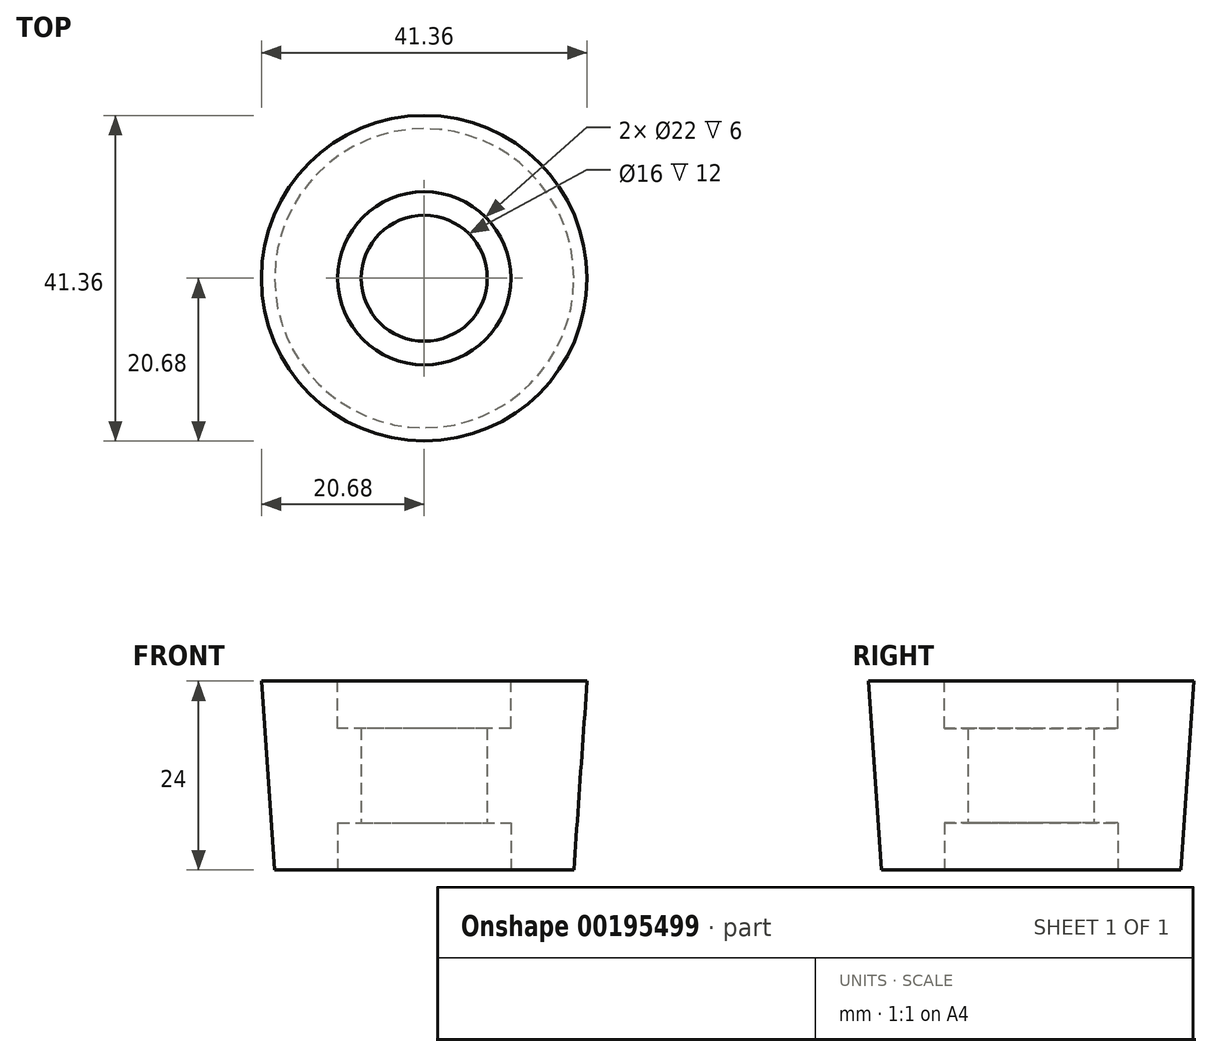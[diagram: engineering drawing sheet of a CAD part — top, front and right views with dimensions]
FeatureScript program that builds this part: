
annotation { "Feature Type Name" : "Feature", "Feature Type Description" : "" }
export const myFeature = defineFeature(function(context is Context, id is Id, definition is map)
    precondition{}
    {
        {
            var Q0;
            Q0=qCreatedBy(makeId("Top.planeOp"),FACE);
            var sketch = newSketch(context, id + "F0", { "sketchPlane" : qUnion([Q0])});
            skCircle(sketch, "E0", {"center": v(0, 0) * mm, "radius": 19 * mm});
            skSolve(sketch);
        }
        {
            var Q0;
            Q0=makeQuery(id+"F0.imprint","IMPRINT",FACE,{"disambiguationData":[TD([[makeQuery(id+"F0.imprint","IMPRINT",EDGE,{"derivedFrom":sQuery(id+"F0.wireOp",EDGE,"E0")}),1.0]])]});
            extrude(context, id + "F1", {"entities" : qUnion([Q0]), "depth" : 24 * mm, "hasDraft" : true, "draftAngle" : 4 * degree});
        }
        {
            var Q0;
            Q0=makeQuery(id+"F1.opExtrude","CAP_FACE",FACE,{"disambiguationData":[OSD([sQuery(id+"F0.wireOp",EDGE,"E0")])],"isStart":true});
            var sketch = newSketch(context, id + "F2", { "sketchPlane" : qUnion([Q0])});
            skCircle(sketch, "E1", {"center": v(0, 0) * mm, "radius": 8 * mm});
            skCircle(sketch, "E2", {"center": v(0, 0) * mm, "radius": 11 * mm});
            skSolve(sketch);
        }
        {
            var Q0;
            Q0=makeQuery(id+"F2.imprint","IMPRINT",FACE,{"disambiguationData":[TD([[makeQuery(id+"F2.imprint","IMPRINT",EDGE,{"derivedFrom":sQuery(id+"F2.wireOp",EDGE,"E1")}),1.0]])]});
            extrude(context, id + "F3", {"entities" : qUnion([Q0]), "operationType" : NewBodyOperationType.REMOVE, "endBound" : BoundingType.THROUGH_ALL, "oppositeDirection" : true, "depth" : 25 * mm});
        }
        {
            var Q0;
            Q0 = qSketchRegion(id + "F2", true);
            extrude(context, id + "F4", {"entities" : qUnion([Q0]), "operationType" : NewBodyOperationType.REMOVE, "oppositeDirection" : true, "depth" : 6 * mm});
        }
        {
            var Q0;
            Q0=makeQuery(id+"F1.opExtrude","CAP_FACE",FACE,{"disambiguationData":[OSD([sQuery(id+"F0.wireOp",EDGE,"E0")])],"isStart":false});
            var sketch = newSketch(context, id + "F5", { "sketchPlane" : qUnion([Q0])});
            skCircle(sketch, "E3", {"center": v(0, 0) * mm, "radius": 11 * mm});
            skSolve(sketch);
        }
        {
            var Q0;
            Q0=makeQuery(id+"F5.imprint","IMPRINT",FACE,{"disambiguationData":[TD([[makeQuery(id+"F5.imprint","IMPRINT",EDGE,{"derivedFrom":sQuery(id+"F5.wireOp",EDGE,"E3")}),1.0]])]});
            extrude(context, id + "F6", {"entities" : qUnion([Q0]), "operationType" : NewBodyOperationType.REMOVE, "oppositeDirection" : true, "depth" : 6 * mm});
        }
    });
